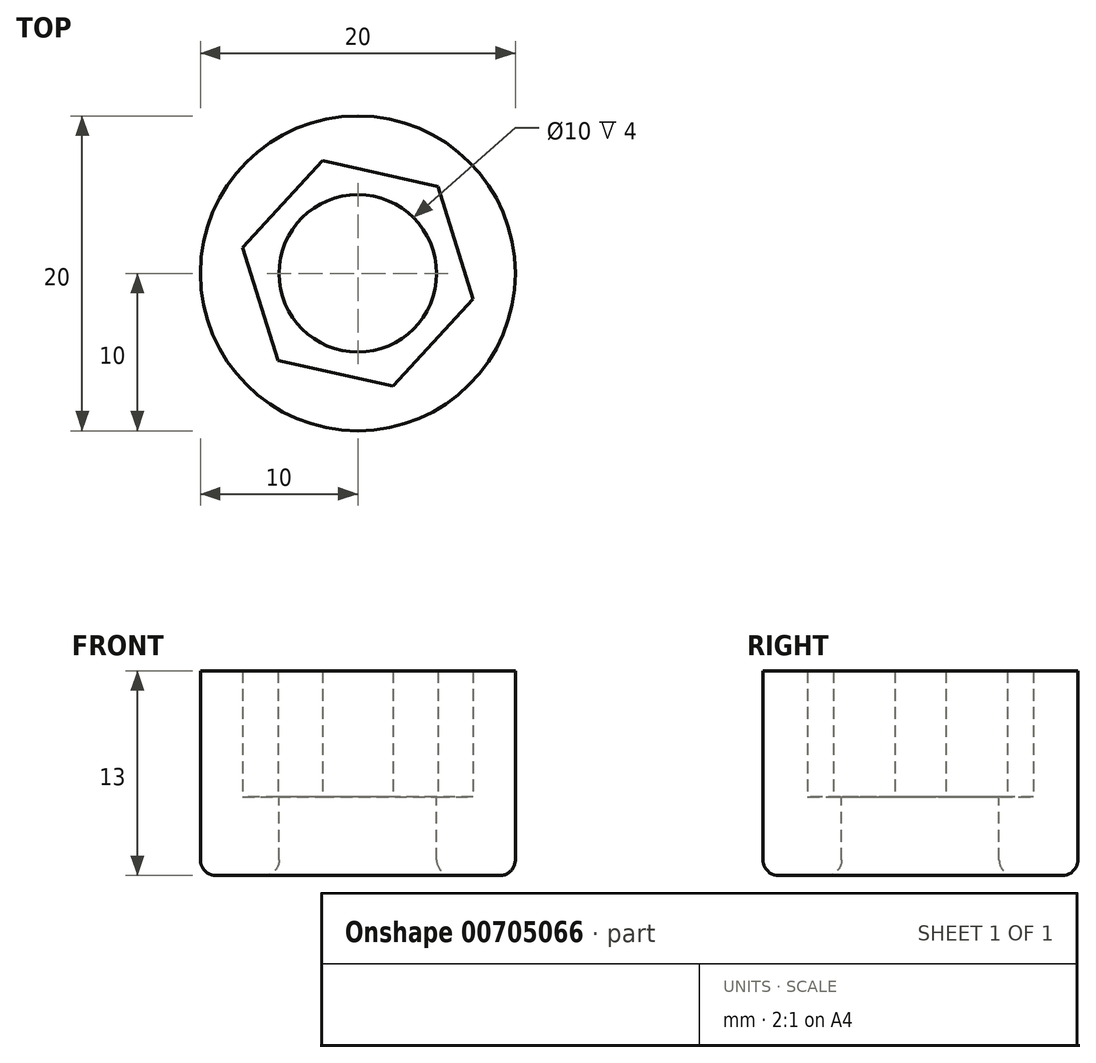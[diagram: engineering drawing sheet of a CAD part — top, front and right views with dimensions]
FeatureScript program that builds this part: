
annotation { "Feature Type Name" : "Feature", "Feature Type Description" : "" }
export const myFeature = defineFeature(function(context is Context, id is Id, definition is map)
    precondition{}
    {
        {
            var Q0;
            Q0=qCreatedBy(makeId("Top.planeOp"),FACE);
            var sketch = newSketch(context, id + "F0", { "sketchPlane" : qUnion([Q0])});
            skCircle(sketch, "E0.cCircle", {"center": v(0, 0) * mm, "radius": 6.5 * mm, "construction": true});
            skLineSegment(sketch, "E0.0", {"start": v(-2.25, 7.16) * mm, "end": v(5.08, 5.53) * mm});
            skLineSegment(sketch, "E0.1", {"start": v(5.08, 5.53) * mm, "end": v(7.33, -1.63) * mm});
            skLineSegment(sketch, "E0.2", {"start": v(7.33, -1.63) * mm, "end": v(2.25, -7.16) * mm});
            skLineSegment(sketch, "E0.3", {"start": v(2.25, -7.16) * mm, "end": v(-5.08, -5.53) * mm});
            skLineSegment(sketch, "E0.4", {"start": v(-5.08, -5.53) * mm, "end": v(-7.33, 1.63) * mm});
            skLineSegment(sketch, "E0.5", {"start": v(-7.33, 1.63) * mm, "end": v(-2.25, 7.16) * mm});
            skPoint(sketch, "E0.0.midPoint", {"position": v(1.41, 6.34) * mm});
            skCircle(sketch, "E1", {"center": v(0, 0) * mm, "radius": 10 * mm});
            skCircle(sketch, "E2", {"center": v(0, 0) * mm, "radius": 5 * mm});
            skSolve(sketch);
        }
        {
            var Q0;
            Q0=makeQuery(id+"F0.imprint","IMPRINT",FACE,{"disambiguationData":[TD([[makeQuery(id+"F0.imprint","IMPRINT",EDGE,{"derivedFrom":sQuery(id+"F0.wireOp",EDGE,"E0.0")}),1.0]])]});
            var Q1;
            Q1=makeQuery(id+"F0.imprint","IMPRINT",FACE,{"disambiguationData":[TD([[makeQuery(id+"F0.imprint","IMPRINT",EDGE,{"derivedFrom":sQuery(id+"F0.wireOp",EDGE,"E0.0")}),-1.0]])]});
            extrude(context, id + "F1", {"entities" : qUnion([Q0, Q1]), "oppositeDirection" : true, "depth" : 5 * mm, "offsetDistance" : 25 * mm});
        }
        {
            var Q0;
            Q0=makeQuery(id+"F0.imprint","IMPRINT",FACE,{"disambiguationData":[TD([[makeQuery(id+"F0.imprint","IMPRINT",EDGE,{"derivedFrom":sQuery(id+"F0.wireOp",EDGE,"E0.0")}),1.0]])]});
            extrude(context, id + "F2", {"entities" : qUnion([Q0]), "operationType" : NewBodyOperationType.ADD, "depth" : 8 * mm, "offsetDistance" : 25 * mm});
        }
        {
            var Q0;
            Q0=makeQuery(id+"F1.opExtrude","CAP_FACE",FACE,{"disambiguationData":[OSD([sQuery(id+"F0.wireOp",EDGE,"E1"),sQuery(id+"F0.wireOp",EDGE,"E2")])],"isStart":false});
            fillet(context, id + "F3", {"entities" : qUnion([Q0]), "radius" : 1 * mm, "tangentPropagation" : true, "allowEdgeOverflow" : false});
        }
    });
